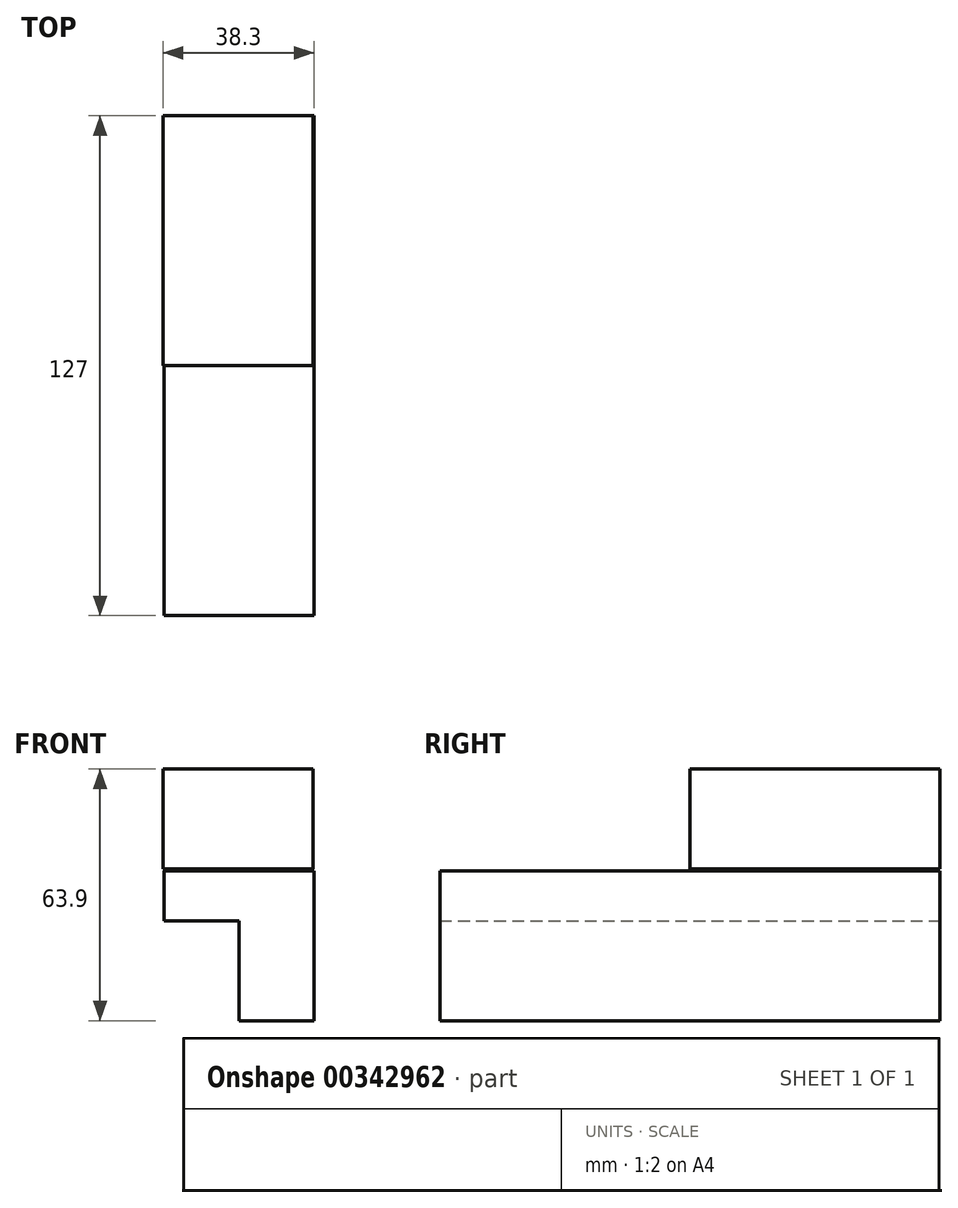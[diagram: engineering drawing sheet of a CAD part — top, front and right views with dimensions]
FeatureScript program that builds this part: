
annotation { "Feature Type Name" : "Feature", "Feature Type Description" : "" }
export const myFeature = defineFeature(function(context is Context, id is Id, definition is map)
    precondition{}
    {
        {
            var Q0;
            Q0=qCreatedBy(makeId("Front.planeOp"),FACE);
            var sketch = newSketch(context, id + "F0", { "sketchPlane" : qUnion([Q0])});
            skLineSegment(sketch, "E0", {"start": v(14.1, -33.08) * mm, "end": v(33.14, -33.08) * mm});
            skLineSegment(sketch, "E1", {"start": v(14.1, -33.08) * mm, "end": v(14.1, -7.68) * mm});
            skLineSegment(sketch, "E2", {"start": v(14.1, -7.68) * mm, "end": v(-4.96, -7.68) * mm});
            skLineSegment(sketch, "E3", {"start": v(-4.96, -7.68) * mm, "end": v(-4.96, 5.02) * mm});
            skLineSegment(sketch, "E4", {"start": v(-4.96, 5.02) * mm, "end": v(33.14, 5.02) * mm});
            skLineSegment(sketch, "E5", {"start": v(33.14, 5.02) * mm, "end": v(33.14, -33.08) * mm});
            skSolve(sketch);
        }
        {
            var Q0;
            Q0 = qSketchRegion(id + "F0", true);
            extrude(context, id + "F1", {"entities" : qUnion([Q0]), "depth" : 127 * mm});
        }
        {
            var Q0;
            Q0=qCreatedBy(makeId("Front.planeOp"),FACE);
            var sketch = newSketch(context, id + "F2", { "sketchPlane" : qUnion([Q0])});
            skPoint(sketch, "E6.start.orphan", {"position": v(0, 5.14) * mm});
            skLineSegment(sketch, "E7", {"start": v(-5.16, 5.42) * mm, "end": v(32.94, 5.42) * mm});
            skLineSegment(sketch, "E8", {"start": v(-5.16, 5.42) * mm, "end": v(-5.16, 30.82) * mm});
            skLineSegment(sketch, "E9", {"start": v(-5.16, 30.82) * mm, "end": v(32.94, 30.82) * mm});
            skLineSegment(sketch, "E10", {"start": v(32.94, 30.82) * mm, "end": v(32.94, 5.42) * mm});
            skSolve(sketch);
        }
        {
            var Q0;
            Q0 = qSketchRegion(id + "F2", true);
            extrude(context, id + "F3", {"entities" : qUnion([Q0]), "depth" : 33.27 * mm});
        }
        {
            var Q0;
            Q0 = qSketchRegion(id + "F2", true);
            extrude(context, id + "F4", {"entities" : qUnion([Q0]), "operationType" : NewBodyOperationType.ADD, "depth" : 63.5 * mm});
        }
    });
